# Revit family: 15085 Стул для кафе и ресторанов Хоббика
name_source: partatom
category: Антураж
revit_build: Autodesk Revit 2018 (Build: 20180423_1000(x64)
units: mm (PartAtom-declared; Revit-internal decimal feet)

## family parameters
Всегда вертикально = Да
Источник визуального образа = Геометрия семейства
На основе рабочей плоскости = Нет
Общий = Нет
При загрузке вырезать с полостями = Нет
Точка расчета площади = Нет

## types (2) — shared parameters
URL = https://hobbyka.ru
Артикул товара = Арт. 15085
Высота = 880 мм
Группа модели = Кресла садовые
Длина = 400 мм
Изготовитель = ООО «Хоббика»
Изображение типоразмера = Стул для кафе и ресторанов Арт 15085.jpg
Материал изделия = Сталь, дерево
Цвет каркаса = Сталь
Ширина = 500 мм

## per-type parameters (varying)
| type | Версия "Дуб" | Версия "Ясень" | Описание | Цвет сидения |
| Версия "Ясень" | Нет | Да | Стул для кафе и ресторанов. Версия "Ясень" | Ясень |
| Версия "Дуб" | Да | Нет | Стул для кафе и ресторанов. Версия "Дуб" | Дуб |
